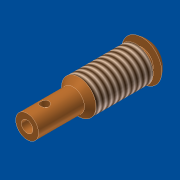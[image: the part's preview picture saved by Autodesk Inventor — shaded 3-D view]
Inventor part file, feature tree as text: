
AUTODESK INVENTOR PART (.ipt)
format: ipt  version: unknown  size: 195,584 bytes
history: native  units: mm
features: sketch x2, revolve x1, extrude x1, thread x1
ambient origin geometry x8: Origin, YZ Plane, XZ Plane, XY Plane, X Axis, Y Axis, Z Axis, Center Point
feature tree (5):
  revolve  "Revolution1"  [1 undecoded]
  extrude  "Extrusion1"  Depth=10.0mm TaperAngle=0.0deg
  thread  "Thread1"  [1 undecoded]
  sketch  "Sketch1"  dims[d0=90.0deg d1=3.0mm]
  sketch  "Sketch2"  dims[d2=1.5mm d3=10.0mm d4=0.0mm d5=10.0mm d6=0.0mm]
note: 2 required parameter values undecoded (feature->parameter linkage not recoverable at this tier; creation-order binding heuristic only, values carry confidence <= 0.55)